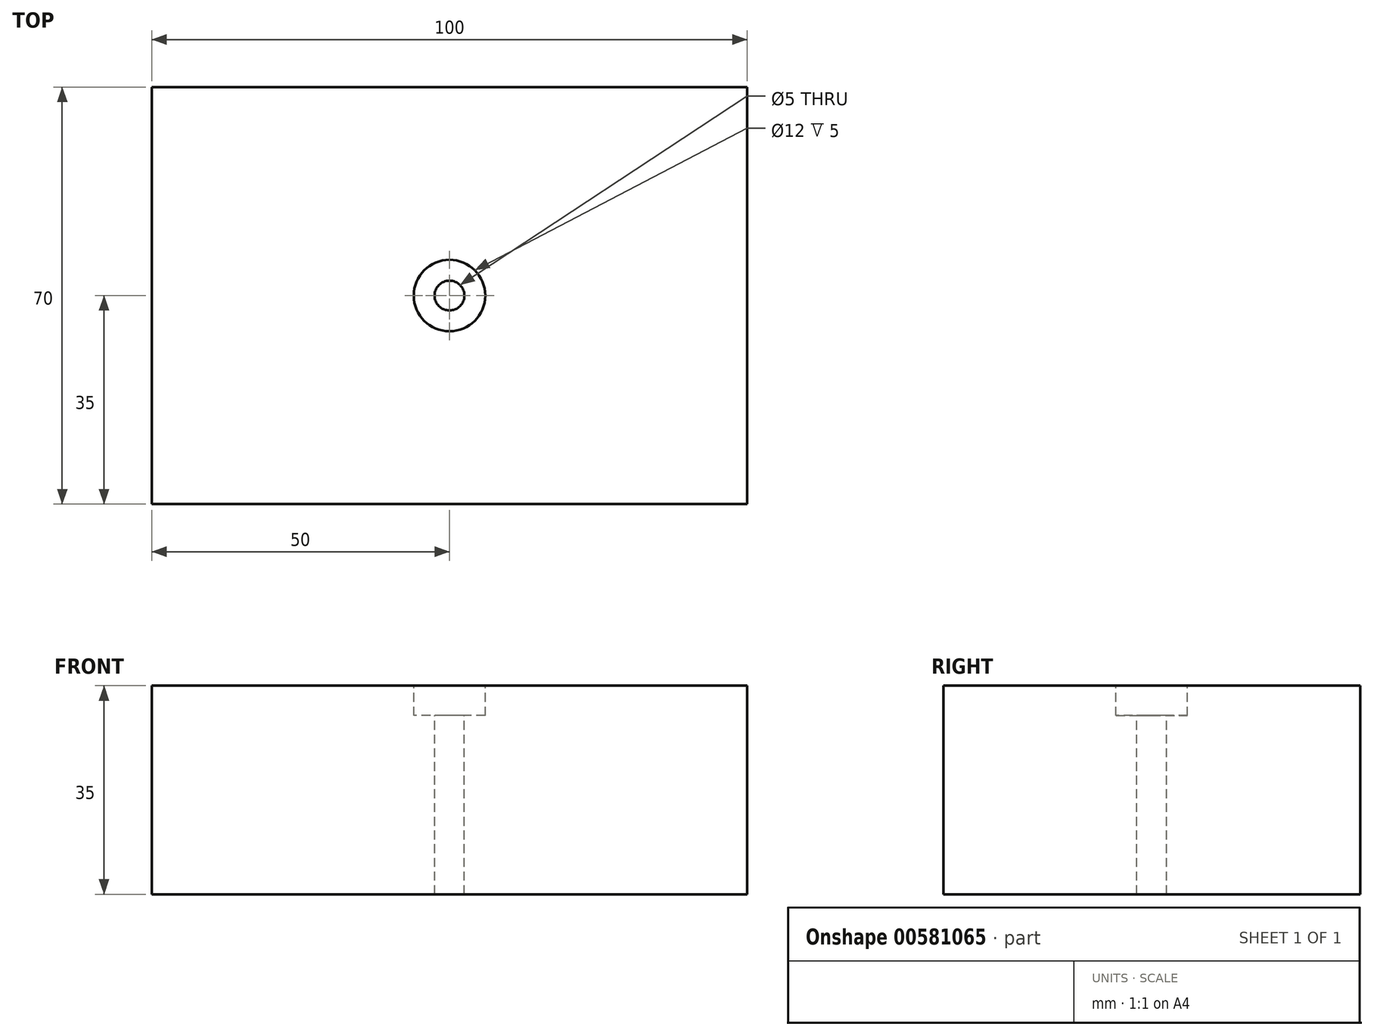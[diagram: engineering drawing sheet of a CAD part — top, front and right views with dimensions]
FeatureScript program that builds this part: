
annotation { "Feature Type Name" : "Feature", "Feature Type Description" : "" }
export const myFeature = defineFeature(function(context is Context, id is Id, definition is map)
    precondition{}
    {
        {
            var Q0;
            Q0=qCreatedBy(makeId("Top.planeOp"),FACE);
            var sketch = newSketch(context, id + "F0", { "sketchPlane" : qUnion([Q0])});
            skLineSegment(sketch, "E0.bottom", {"start": v(-50, 35) * mm, "end": v(50, 35) * mm});
            skLineSegment(sketch, "E0.top", {"start": v(-50, -35) * mm, "end": v(50, -35) * mm});
            skLineSegment(sketch, "E0.left", {"start": v(-50, 35) * mm, "end": v(-50, -35) * mm});
            skLineSegment(sketch, "E0.right", {"start": v(50, 35) * mm, "end": v(50, -35) * mm});
            skSolve(sketch);
        }
        {
            var Q0;
            Q0=makeQuery(id+"F0.imprint","IMPRINT",FACE,{"disambiguationData":[TD([[makeQuery(id+"F0.imprint","IMPRINT",EDGE,{"derivedFrom":sQuery(id+"F0.wireOp",EDGE,"E0.bottom")}),-1.0]])]});
            extrude(context, id + "F1", {"entities" : qUnion([Q0]), "endBound" : BoundingType.SYMMETRIC, "depth" : 35 * mm, "offsetDistance" : 25 * mm});
        }
        {
            var Q0;
            Q0=makeQuery(id+"F1.opExtrude","CAP_FACE",FACE,{"disambiguationData":[OSD([sQuery(id+"F0.wireOp",EDGE,"E0.bottom"),sQuery(id+"F0.wireOp",EDGE,"E0.top"),sQuery(id+"F0.wireOp",EDGE,"E0.left"),sQuery(id+"F0.wireOp",EDGE,"E0.right")])],"isStart":false});
            var sketch = newSketch(context, id + "F2", { "sketchPlane" : qUnion([Q0])});
            skPoint(sketch, "E1", {"position": v(0, 0) * mm});
            skSolve(sketch);
        }
        {
            var Q0;
            Q0=sQuery(id+"F2.wireOp",VERTEX,"E1");
            var Q1;
            Q1=makeQuery(id+"F1.opExtrude","SWEPT_BODY",BODY,{"disambiguationData":[OSD([sQuery(id+"F0.wireOp",EDGE,"E0.bottom"),sQuery(id+"F0.wireOp",EDGE,"E0.top"),sQuery(id+"F0.wireOp",EDGE,"E0.left"),sQuery(id+"F0.wireOp",EDGE,"E0.right")])]});
            hole(context, id + "F3", {"style" : HoleStyle.C_BORE, "endStyle" : HoleEndStyle.THROUGH, "holeDiameter" : 5 * mm, "cBoreDiameter" : 12 * mm, "cBoreDepth" : 5 * mm, "majorDiameter" : 5 * mm, "isTappedThrough" : true, "tappedDepth" : 12 * mm, "tapClearance" : 3, "locations" : qUnion([Q0]), "scope" : qUnion([Q1])});
        }
    });
